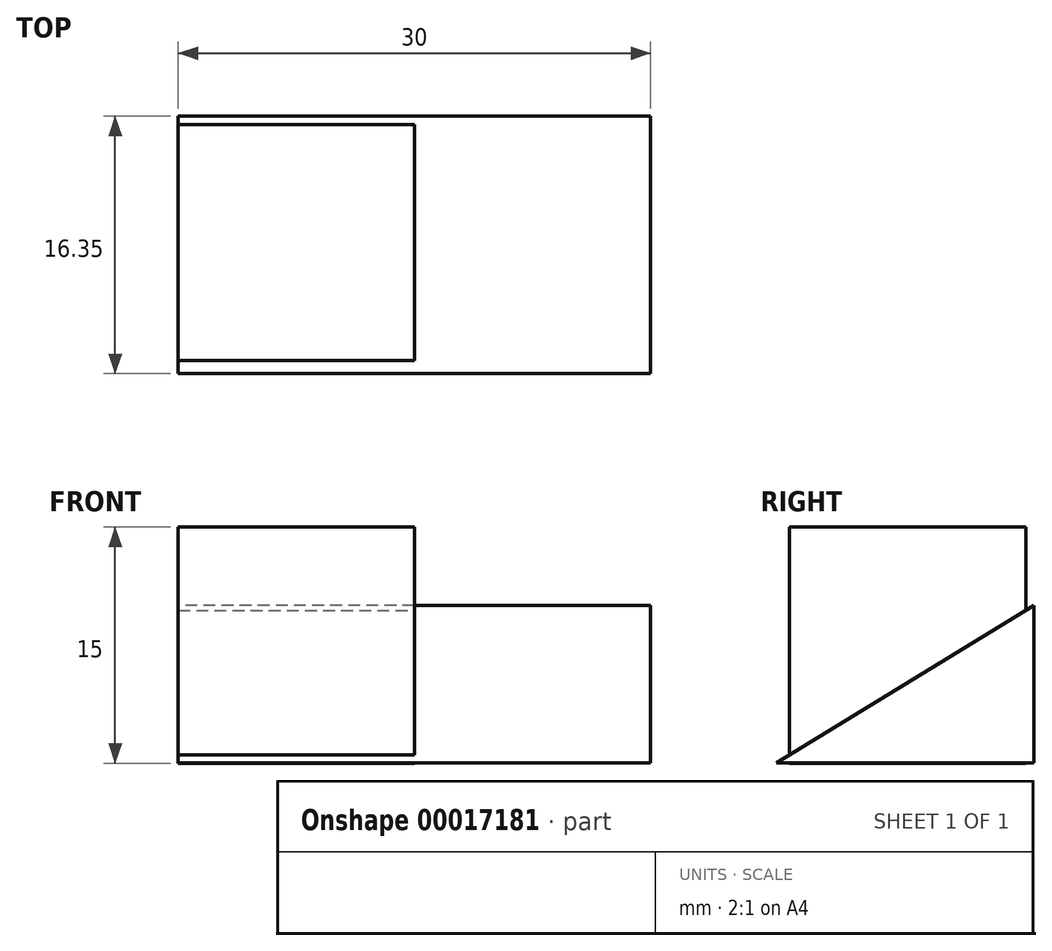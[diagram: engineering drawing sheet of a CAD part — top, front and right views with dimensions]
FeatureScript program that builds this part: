
annotation { "Feature Type Name" : "Feature", "Feature Type Description" : "" }
export const myFeature = defineFeature(function(context is Context, id is Id, definition is map)
    precondition{}
    {
        {
            var Q0;
            Q0=qCreatedBy(makeId("Right.planeOp"),FACE);
            var sketch = newSketch(context, id + "F0", { "sketchPlane" : qUnion([Q0])});
            skLineSegment(sketch, "E0.bottom", {"start": v(-9.27, 14.98) * mm, "end": v(5.73, 14.98) * mm});
            skLineSegment(sketch, "E0.top", {"start": v(-9.27, -0.02) * mm, "end": v(5.73, -0.02) * mm});
            skLineSegment(sketch, "E0.left", {"start": v(-9.27, 14.98) * mm, "end": v(-9.27, -0.02) * mm});
            skLineSegment(sketch, "E0.right", {"start": v(5.73, 14.98) * mm, "end": v(5.73, -0.02) * mm});
            skSolve(sketch);
        }
        {
            var Q0;
            Q0 = qSketchRegion(id + "F0", true);
            extrude(context, id + "F1", {"entities" : qUnion([Q0]), "depth" : 15 * mm});
        }
        {
            var Q0;
            Q0=qCreatedBy(makeId("Right.planeOp"),FACE);
            var sketch = newSketch(context, id + "F2", { "sketchPlane" : qUnion([Q0])});
            skLineSegment(sketch, "E1", {"start": v(-10.1, 0) * mm, "end": v(6.25, 10) * mm});
            skLineSegment(sketch, "E2", {"start": v(6.25, 10) * mm, "end": v(6.25, 0) * mm});
            skLineSegment(sketch, "E3", {"start": v(-10.1, 0) * mm, "end": v(6.25, 0) * mm});
            skSolve(sketch);
        }
        {
            var Q0;
            Q0 = qSketchRegion(id + "F2", true);
            extrude(context, id + "F3", {"entities" : qUnion([Q0]), "operationType" : NewBodyOperationType.ADD, "depth" : 30 * mm});
        }
    });
